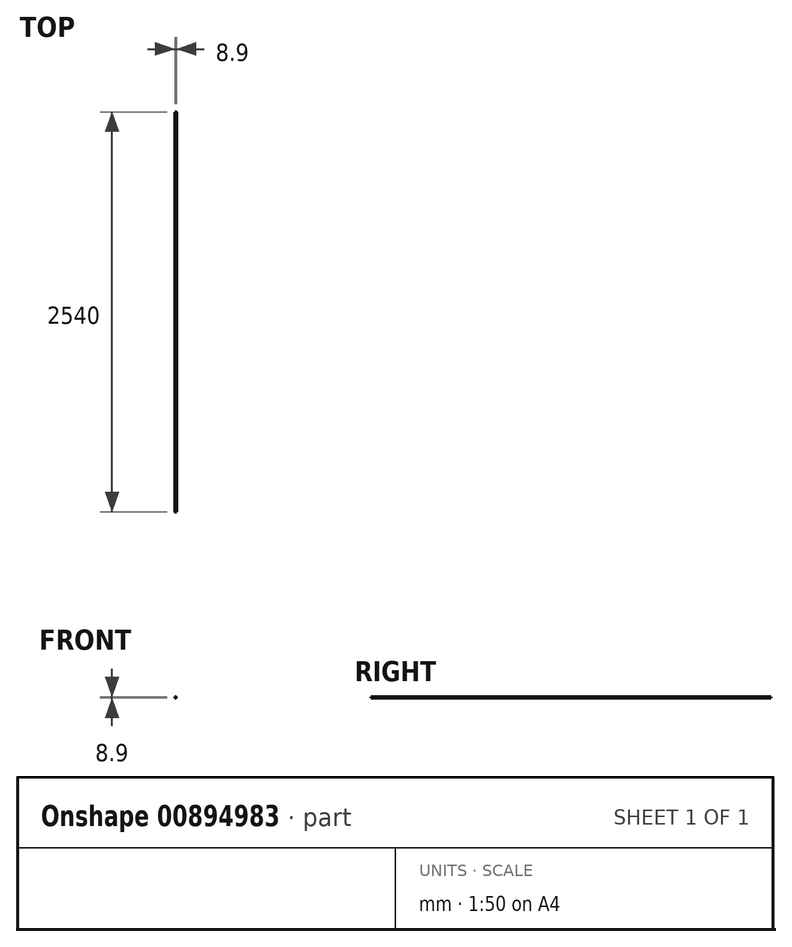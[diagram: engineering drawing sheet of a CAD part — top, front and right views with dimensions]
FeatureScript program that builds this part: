
annotation { "Feature Type Name" : "Feature", "Feature Type Description" : "" }
export const myFeature = defineFeature(function(context is Context, id is Id, definition is map)
    precondition{}
    {
        {
            var Q0;
            Q0=qCreatedBy(makeId("Front.planeOp"),FACE);
            var sketch = newSketch(context, id + "F0", { "sketchPlane" : qUnion([Q0])});
            skCircle(sketch, "E0", {"center": v(0, 0) * mm, "radius": 4.45 * mm});
            skSolve(sketch);
        }
        {
            var Q0;
            Q0=makeQuery(id+"F0.imprint","IMPRINT",FACE,{"disambiguationData":[TD([[makeQuery(id+"F0.imprint","IMPRINT",EDGE,{"derivedFrom":sQuery(id+"F0.wireOp",EDGE,"E0")}),1.0]])]});
            var Q1;
            Q1=sQuery(id+"F0.wireOp",EDGE,"E0");
            extrude(context, id + "F1", {"entities" : qUnion([Q0]), "surfaceEntities" : qUnion([Q1]), "endBound" : BoundingType.SYMMETRIC, "oppositeDirection" : true, "depth" : 2540 * mm, "offsetDistance" : 25.4 * mm});
        }
    });
